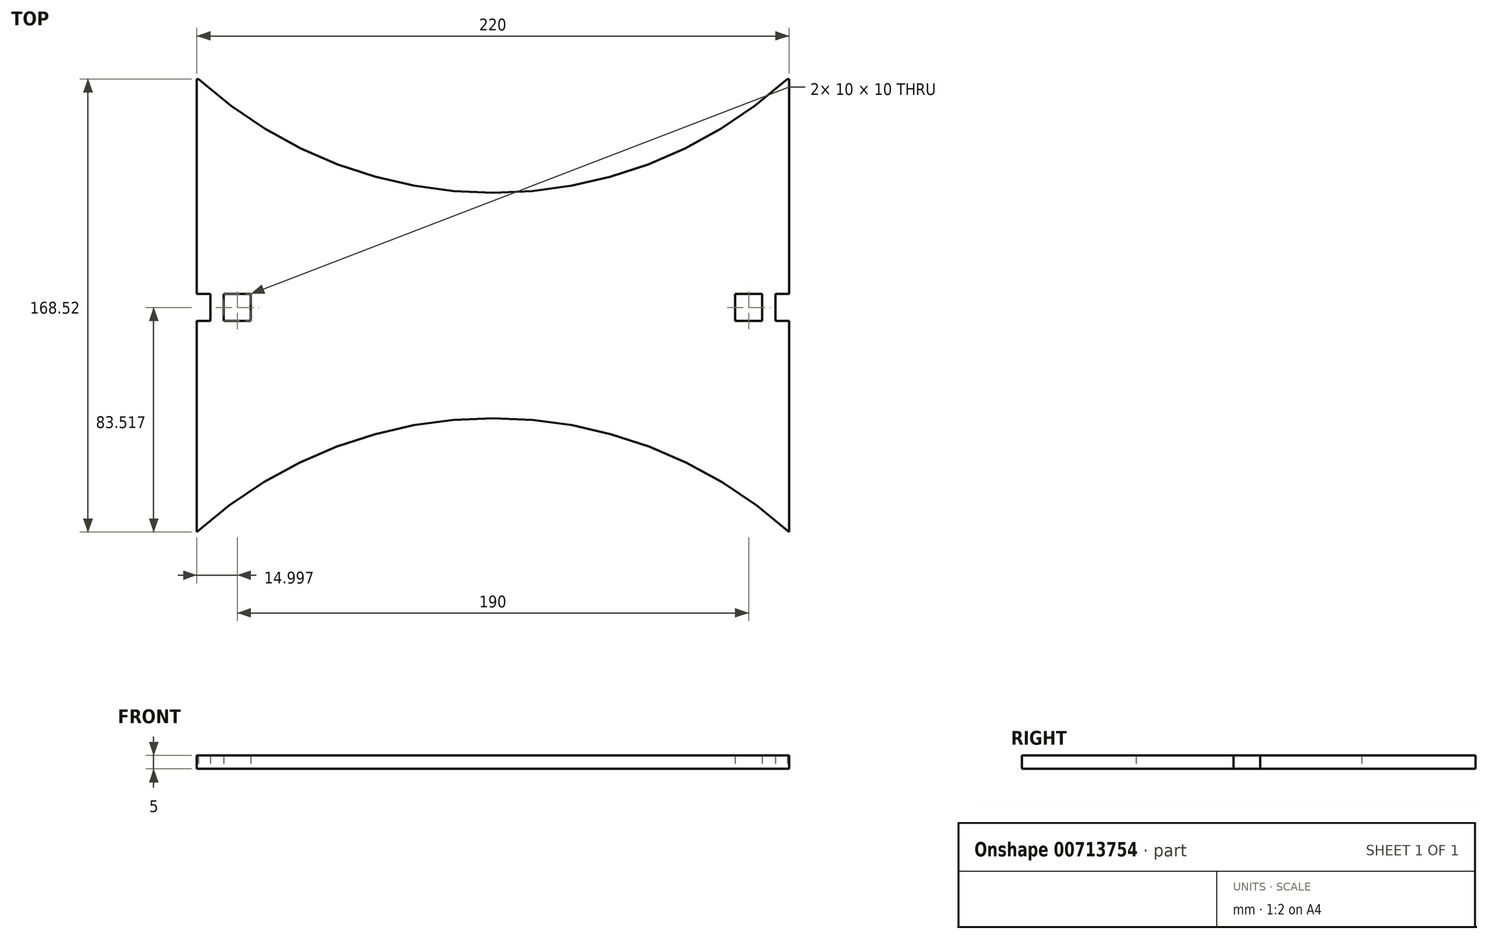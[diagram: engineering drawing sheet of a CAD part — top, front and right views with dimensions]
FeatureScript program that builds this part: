
annotation { "Feature Type Name" : "Feature", "Feature Type Description" : "" }
export const myFeature = defineFeature(function(context is Context, id is Id, definition is map)
    precondition{}
    {
        {
            var Q0;
            Q0=qCreatedBy(makeId("Top.planeOp"),FACE);
            var sketch = newSketch(context, id + "F0", { "sketchPlane" : qUnion([Q0])});
            skLineSegment(sketch, "E0.top", {"start": v(-218.4, 298.15) * mm, "end": v(-217.77, 298.15) * mm});
            skLineSegment(sketch, "E0.left", {"start": v(-218.4, 128.15) * mm, "end": v(-218.4, 208.15) * mm});
            skLineSegment(sketch, "E0.right", {"start": v(1.6, 128.15) * mm, "end": v(1.6, 208.15) * mm});
            skLineSegment(sketch, "E1", {"start": v(-218.4, 298.15) * mm, "end": v(-218.4, 218.15) * mm});
            skLineSegment(sketch, "E2", {"start": v(-218.4, 218.15) * mm, "end": v(-213.4, 218.15) * mm});
            skLineSegment(sketch, "E3", {"start": v(-213.4, 218.15) * mm, "end": v(-218.4, 218.15) * mm});
            skLineSegment(sketch, "E4", {"start": v(-218.4, 208.15) * mm, "end": v(-213.4, 208.15) * mm});
            skLineSegment(sketch, "E5", {"start": v(-213.4, 208.15) * mm, "end": v(-213.4, 218.15) * mm});
            skLineSegment(sketch, "E6", {"start": v(1.6, 298.15) * mm, "end": v(1.6, 218.15) * mm});
            skLineSegment(sketch, "E7", {"start": v(1.6, 208.15) * mm, "end": v(-3.4, 208.15) * mm});
            skLineSegment(sketch, "E8.bottom", {"start": v(-208.4, 218.15) * mm, "end": v(-198.4, 218.15) * mm});
            skLineSegment(sketch, "E8.top", {"start": v(-208.4, 208.15) * mm, "end": v(-198.4, 208.15) * mm});
            skLineSegment(sketch, "E8.left", {"start": v(-208.4, 218.15) * mm, "end": v(-208.4, 208.15) * mm});
            skLineSegment(sketch, "E8.right", {"start": v(-198.4, 218.15) * mm, "end": v(-198.4, 208.15) * mm});
            skLineSegment(sketch, "E9.trimOffspring", {"start": v(-218.4, 218.15) * mm, "end": v(-218.4, 298.15) * mm});
            skLineSegment(sketch, "E10", {"start": v(-3.4, 208.15) * mm, "end": v(-3.4, 218.15) * mm});
            skLineSegment(sketch, "E11", {"start": v(-3.4, 218.15) * mm, "end": v(1.6, 218.15) * mm});
            skLineSegment(sketch, "E12.bottom", {"start": v(-8.4, 208.15) * mm, "end": v(-18.4, 208.15) * mm});
            skLineSegment(sketch, "E12.top", {"start": v(-8.4, 218.15) * mm, "end": v(-18.4, 218.15) * mm});
            skLineSegment(sketch, "E12.left", {"start": v(-8.4, 208.15) * mm, "end": v(-8.4, 218.15) * mm});
            skLineSegment(sketch, "E12.right", {"start": v(-18.4, 208.15) * mm, "end": v(-18.4, 218.15) * mm});
            skLineSegment(sketch, "E13.trimOffspring", {"start": v(1.6, 218.15) * mm, "end": v(1.6, 298.15) * mm});
            skArc(sketch, "E14", {"start": v(-217.77, 298.15) * mm, "mid": v(-108.4, 255.78) * mm, "end": v(0.99, 298.15) * mm});
            skArc(sketch, "E15", {"start": v(1.6, 129.63) * mm, "mid": v(-108.4, 172.03) * mm, "end": v(-218.4, 129.63) * mm});
            skLineSegment(sketch, "E16.trimOffspring", {"start": v(0.99, 298.15) * mm, "end": v(1.6, 298.15) * mm});
            skSolve(sketch);
        }
        {
            var Q0;
            Q0 = qSketchRegion(id + "F0", true);
            var Q1;
            {var subQ0=sQuery(id+"F0.wireOp",EDGE,"E4");Q1=makeQuery(id+"F0.imprint","IMPRINT",FACE,{"disambiguationData":[TD([[makeQuery(id+"F0.imprint","IMPRINT",EDGE,{"derivedFrom":subQ0}),-1.0]])]});}
            extrude(context, id + "F1", {"entities" : qUnion([Q0, Q1]), "depth" : 5 * mm, "offsetDistance" : 25 * mm});
        }
    });
